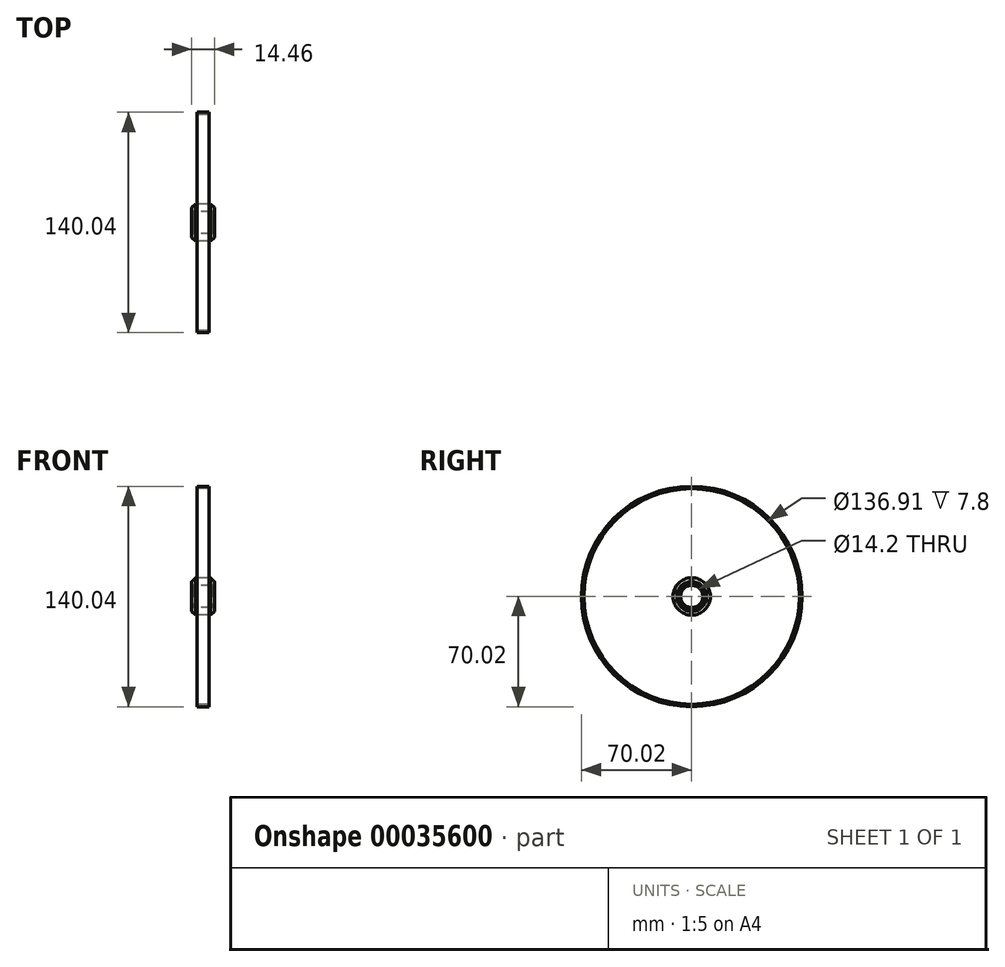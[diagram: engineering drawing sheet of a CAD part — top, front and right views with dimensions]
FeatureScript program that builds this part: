
annotation { "Feature Type Name" : "Feature", "Feature Type Description" : "" }
export const myFeature = defineFeature(function(context is Context, id is Id, definition is map)
    precondition{}
    {
        {
            var Q0;
            Q0=qCreatedBy(makeId("Front.planeOp"),FACE);
            var sketch = newSketch(context, id + "F0", { "sketchPlane" : qUnion([Q0])});
            skLineSegment(sketch, "E0", {"start": v(0, 68.45) * mm, "end": v(3.9, 68.45) * mm});
            skLineSegment(sketch, "E1", {"start": v(0, 70.02) * mm, "end": v(3.9, 70.02) * mm});
            skLineSegment(sketch, "E2", {"start": v(3.9, 70.02) * mm, "end": v(3.9, 68.45) * mm});
            skLineSegment(sketch, "E3.MirrorCS", {"start": v(0, 68.45) * mm, "end": v(-3.9, 68.45) * mm});
            skLineSegment(sketch, "E4.MirrorCS", {"start": v(0, 70.02) * mm, "end": v(-3.9, 70.02) * mm});
            skLineSegment(sketch, "E5.MirrorCS", {"start": v(0, 0) * mm, "end": v(0, 68.45) * mm, "construction": true});
            skLineSegment(sketch, "E6.MirrorCS", {"start": v(-3.9, 70.02) * mm, "end": v(-3.9, 68.45) * mm});
            skLineSegment(sketch, "E7", {"start": v(0, 7.1) * mm, "end": v(6.35, 7.1) * mm});
            skLineSegment(sketch, "E8", {"start": v(7.23, 9.47) * mm, "end": v(4.85, 11.85) * mm});
            skLineSegment(sketch, "E9", {"start": v(4.85, 11.85) * mm, "end": v(0, 11.85) * mm});
            skLineSegment(sketch, "E10", {"start": v(0, 11.85) * mm, "end": v(0, 7.1) * mm, "construction": true});
            skLineSegment(sketch, "E11", {"start": v(7.23, 9.47) * mm, "end": v(7.23, 7.97) * mm});
            skLineSegment(sketch, "E12", {"start": v(7.23, 7.97) * mm, "end": v(6.35, 7.1) * mm});
            skPoint(sketch, "E13.orphan", {"position": v(9.6, 7.1) * mm});
            skLineSegment(sketch, "E14.MirrorCS", {"start": v(-7.23, 7.97) * mm, "end": v(-6.35, 7.1) * mm});
            skLineSegment(sketch, "E15.MirrorCS", {"start": v(-7.23, 9.47) * mm, "end": v(-7.23, 7.97) * mm});
            skPoint(sketch, "E16.MirrorP", {"position": v(-9.6, 7.1) * mm});
            skLineSegment(sketch, "E17.MirrorCS", {"start": v(-4.85, 11.85) * mm, "end": v(0, 11.85) * mm});
            skLineSegment(sketch, "E18.MirrorCS", {"start": v(-7.23, 9.47) * mm, "end": v(-4.85, 11.85) * mm});
            skLineSegment(sketch, "E19.MirrorCS", {"start": v(0, 7.1) * mm, "end": v(-6.35, 7.1) * mm});
            skLineSegment(sketch, "E20", {"start": v(0, 0) * mm, "end": v(37.2, 0) * mm, "construction": true});
            skSolve(sketch);
        }
        {
            var Q0;
            Q0=makeQuery(id+"F0.imprint","IMPRINT",FACE,{"disambiguationData":[TD([[makeQuery(id+"F0.imprint","IMPRINT",EDGE,{"derivedFrom":sQuery(id+"F0.wireOp",EDGE,"E7")}),1.0]])]});
            var Q1;
            Q1=makeQuery(id+"F0.imprint","IMPRINT",FACE,{"disambiguationData":[TD([[makeQuery(id+"F0.imprint","IMPRINT",EDGE,{"derivedFrom":sQuery(id+"F0.wireOp",EDGE,"E0")}),1.0]])]});
            var Q2;
            Q2=sQuery(id+"F0.wireOp",EDGE,"E20");
            revolve(context, id + "F1", {"entities" : qUnion([Q0, Q1]), "axis" : qUnion([Q2]), "revolveType" : RevolveType.FULL});
        }
    });
